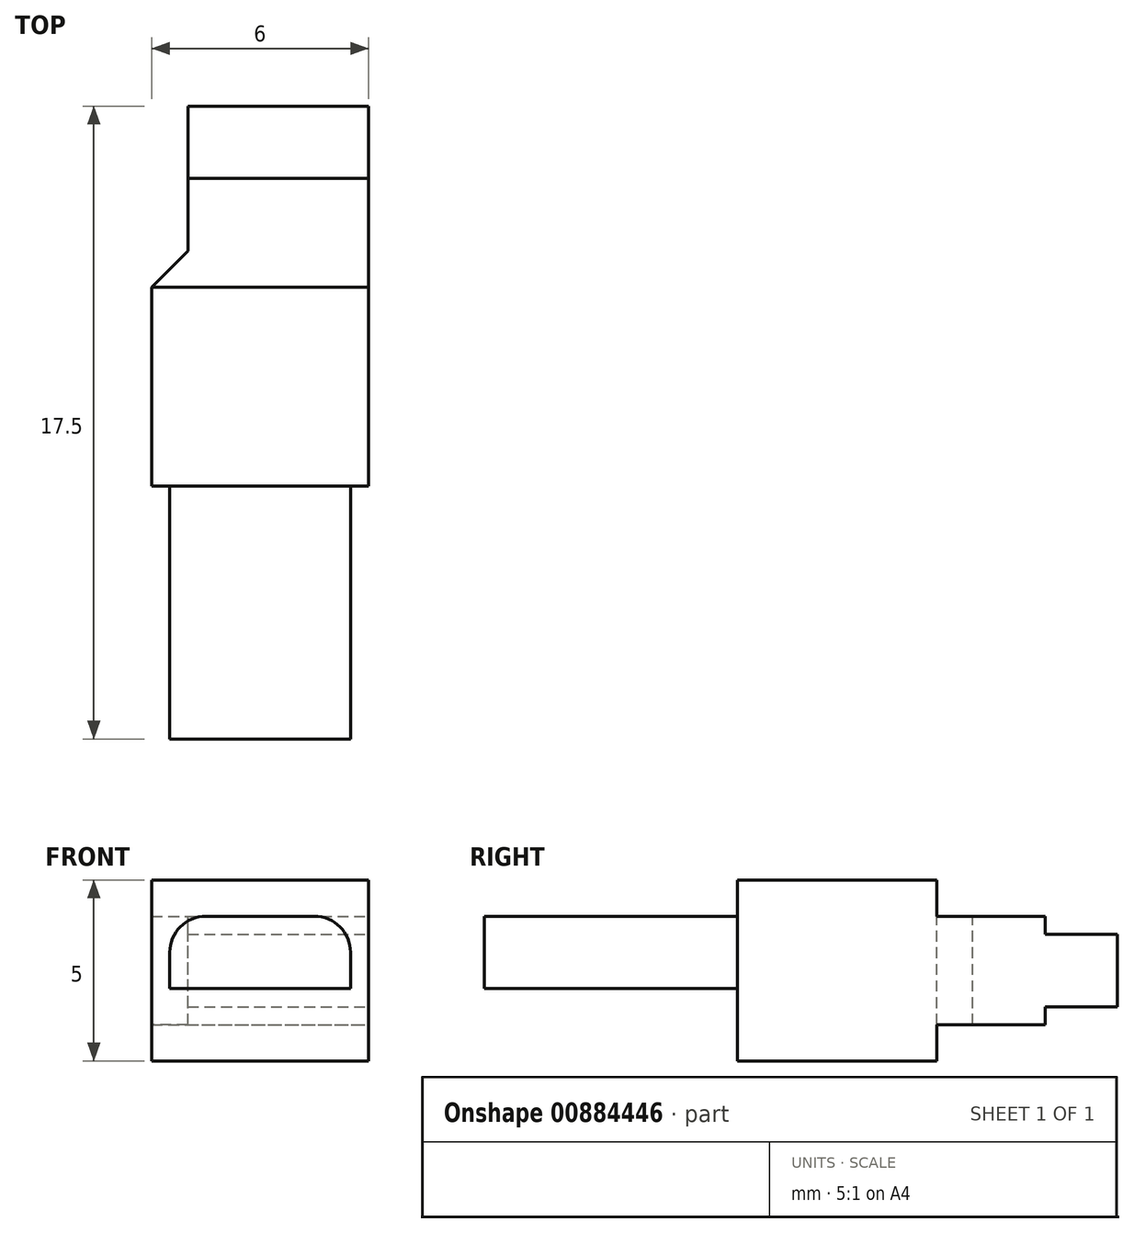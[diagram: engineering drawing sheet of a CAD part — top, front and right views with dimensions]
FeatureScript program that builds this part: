
annotation { "Feature Type Name" : "Feature", "Feature Type Description" : "" }
export const myFeature = defineFeature(function(context is Context, id is Id, definition is map)
    precondition{}
    {
        {
            var Q0;
            Q0=qCreatedBy(makeId("Front.planeOp"),FACE);
            var sketch = newSketch(context, id + "F0", { "sketchPlane" : qUnion([Q0])});
            skLineSegment(sketch, "E0.bottom", {"start": v(2.5, -1) * mm, "end": v(-2.5, -1) * mm});
            skLineSegment(sketch, "E0.top", {"start": v(1.5, 1) * mm, "end": v(-1.5, 1) * mm});
            skLineSegment(sketch, "E0.left", {"start": v(2.5, -1) * mm, "end": v(2.5, 0) * mm});
            skLineSegment(sketch, "E0.right", {"start": v(-2.5, -1) * mm, "end": v(-2.5, 0) * mm});
            skPoint(sketch, "E0.middle", {"position": v(0, 0) * mm});
            skPoint(sketch, "E1.visualSharp", {"position": v(-2.5, 1) * mm});
            skArc(sketch, "E1.filletArc", {"start": v(-1.5, 1) * mm, "mid": v(-2.2, 0.7) * mm, "end": v(-2.5, 0) * mm});
            skPoint(sketch, "E2.visualSharp", {"position": v(2.5, 1) * mm});
            skArc(sketch, "E2.filletArc", {"start": v(2.5, 0) * mm, "mid": v(2.2, 0.7) * mm, "end": v(1.5, 1) * mm});
            skSolve(sketch);
        }
        {
            var Q0;
            Q0=makeQuery(id+"F0.imprint","IMPRINT",FACE,{"disambiguationData":[TD([[makeQuery(id+"F0.imprint","IMPRINT",EDGE,{"derivedFrom":sQuery(id+"F0.wireOp",EDGE,"E0.bottom")}),-1.0]])]});
            extrude(context, id + "F1", {"entities" : qUnion([Q0]), "depth" : 7 * mm, "offsetDistance" : 25 * mm});
        }
        {
            var Q0;
            Q0=makeQuery(id+"F1.opExtrude","CAP_FACE",FACE,{"disambiguationData":[OSD([sQuery(id+"F0.wireOp",EDGE,"E0.bottom"),sQuery(id+"F0.wireOp",EDGE,"E0.top"),sQuery(id+"F0.wireOp",EDGE,"E0.left"),sQuery(id+"F0.wireOp",EDGE,"E0.right"),sQuery(id+"F0.wireOp",EDGE,"E1.filletArc"),sQuery(id+"F0.wireOp",EDGE,"E2.filletArc")])],"isStart":true});
            var sketch = newSketch(context, id + "F2", { "sketchPlane" : qUnion([Q0])});
            skLineSegment(sketch, "E3.bottom", {"start": v(3, -3) * mm, "end": v(-3, -3) * mm});
            skLineSegment(sketch, "E3.top", {"start": v(3, 2) * mm, "end": v(-3, 2) * mm});
            skLineSegment(sketch, "E3.left", {"start": v(3, -3) * mm, "end": v(3, 2) * mm});
            skLineSegment(sketch, "E3.right", {"start": v(-3, -3) * mm, "end": v(-3, 2) * mm});
            skPoint(sketch, "E3.middle", {"position": v(0, -0.5) * mm});
            skSolve(sketch);
        }
        {
            var Q0;
            Q0=makeQuery(id+"F2.imprint","IMPRINT",FACE,{"disambiguationData":[TD([[makeQuery(id+"F2.imprint","IMPRINT",EDGE,{"derivedFrom":sQuery(id+"F2.wireOp",EDGE,"E3.bottom")}),-1.0]])]});
            var Q1;
            Q1=makeQuery(id+"F2.imprint","IMPRINT",FACE,{"disambiguationData":[TD([[makeQuery(id+"F2.imprint","IMPRINT",EDGE,{"derivedFrom":makeQuery(id+"F1.opExtrude","CAP_EDGE",EDGE,{"disambiguationData":[OSD([sQuery(id+"F0.wireOp",EDGE,"E0.bottom")])],"isStart":true})}),1.0]])]});
            extrude(context, id + "F3", {"entities" : qUnion([Q0, Q1]), "operationType" : NewBodyOperationType.ADD, "depth" : 5.5 * mm, "offsetDistance" : 25 * mm});
        }
        {
            var Q0;
            Q0=makeQuery(id+"F3.opExtrude","CAP_FACE",FACE,{"disambiguationData":[OSD([sQuery(id+"F2.wireOp",EDGE,"E3.bottom"),sQuery(id+"F2.wireOp",EDGE,"E3.top"),sQuery(id+"F2.wireOp",EDGE,"E3.left"),sQuery(id+"F2.wireOp",EDGE,"E3.right")])],"isStart":false});
            var sketch = newSketch(context, id + "F4", { "sketchPlane" : qUnion([Q0])});
            skLineSegment(sketch, "E4", {"start": v(3, -0.5) * mm, "end": v(-3, -0.5) * mm, "construction": true});
            skLineSegment(sketch, "E5.bottom", {"start": v(3, 1) * mm, "end": v(-3, 1) * mm});
            skLineSegment(sketch, "E5.top", {"start": v(3, -2) * mm, "end": v(-3, -2) * mm});
            skLineSegment(sketch, "E5.left", {"start": v(3, 1) * mm, "end": v(3, -2) * mm});
            skLineSegment(sketch, "E5.right", {"start": v(-3, 1) * mm, "end": v(-3, -2) * mm});
            skPoint(sketch, "E5.middle", {"position": v(0, -0.5) * mm});
            skSolve(sketch);
        }
        {
            var Q0;
            Q0=makeQuery(id+"F4.imprint","IMPRINT",FACE,{"disambiguationData":[TD([[makeQuery(id+"F4.imprint","IMPRINT",EDGE,{"derivedFrom":sQuery(id+"F4.wireOp",EDGE,"E5.bottom")}),1.0]])]});
            extrude(context, id + "F5", {"entities" : qUnion([Q0]), "operationType" : NewBodyOperationType.ADD, "depth" : 3 * mm, "offsetDistance" : 25 * mm});
        }
        {
            var Q0;
            Q0=makeQuery(id+"F5.opExtrude","CAP_FACE",FACE,{"disambiguationData":[OSD([sQuery(id+"F4.wireOp",EDGE,"E5.bottom"),sQuery(id+"F4.wireOp",EDGE,"E5.top"),sQuery(id+"F4.wireOp",EDGE,"E5.left"),sQuery(id+"F4.wireOp",EDGE,"E5.right")])],"isStart":false});
            var sketch = newSketch(context, id + "F6", { "sketchPlane" : qUnion([Q0])});
            skLineSegment(sketch, "E6", {"start": v(-3, -0.5) * mm, "end": v(3, -0.5) * mm, "construction": true});
            skLineSegment(sketch, "E7.bottom", {"start": v(3, -1.5) * mm, "end": v(-3, -1.5) * mm});
            skLineSegment(sketch, "E7.top", {"start": v(3, 0.5) * mm, "end": v(-3, 0.5) * mm});
            skLineSegment(sketch, "E7.left", {"start": v(3, -1.5) * mm, "end": v(3, 0.5) * mm});
            skLineSegment(sketch, "E7.right", {"start": v(-3, -1.5) * mm, "end": v(-3, 0.5) * mm});
            skPoint(sketch, "E7.middle", {"position": v(0, -0.5) * mm});
            skSolve(sketch);
        }
        {
            var Q0;
            Q0=makeQuery(id+"F6.imprint","IMPRINT",FACE,{"disambiguationData":[TD([[makeQuery(id+"F6.imprint","IMPRINT",EDGE,{"derivedFrom":sQuery(id+"F6.wireOp",EDGE,"E7.bottom")}),-1.0]])]});
            extrude(context, id + "F7", {"entities" : qUnion([Q0]), "operationType" : NewBodyOperationType.ADD, "depth" : 2 * mm, "offsetDistance" : 25 * mm});
        }
        {
            var Q0;
            Q0=makeQuery(id+"F7.boolean.opBoolean","MERGE",FACE,{"derivedFrom":[makeQuery(id+"F5.boolean.opBoolean","MERGE",FACE,{"derivedFrom":[makeQuery(id+"F3.opExtrude","SWEPT_FACE",FACE,{"disambiguationData":[OSD([sQuery(id+"F2.wireOp",EDGE,"E3.left")])]}),makeQuery(id+"F5.opExtrude","SWEPT_FACE",FACE,{"disambiguationData":[OSD([sQuery(id+"F4.wireOp",EDGE,"E5.left")])]})]}),makeQuery(id+"F7.opExtrude","SWEPT_FACE",FACE,{"disambiguationData":[OSD([sQuery(id+"F6.wireOp",EDGE,"E7.left")])]})]});
            var sketch = newSketch(context, id + "F8", { "sketchPlane" : qUnion([Q0])});
            skLineSegment(sketch, "E8.bottom", {"start": v(-5.5, 1) * mm, "end": v(-10.5, 1) * mm});
            skLineSegment(sketch, "E8.top", {"start": v(-5.5, -2) * mm, "end": v(-10.5, -2) * mm});
            skLineSegment(sketch, "E8.left", {"start": v(-5.5, 1) * mm, "end": v(-5.5, -2) * mm});
            skLineSegment(sketch, "E8.right", {"start": v(-10.5, 1) * mm, "end": v(-10.5, -2) * mm});
            skSolve(sketch);
        }
        {
            var Q0;
            {var subQ7=sQuery(id+"F8.wireOp",EDGE,"E8.left");Q0=makeQuery(id+"F8.imprint","IMPRINT",FACE,{"disambiguationData":[TD([[makeQuery(id+"F8.imprint","IMPRINT",EDGE,{"derivedFrom":subQ7}),-1.0]])]});}
            extrude(context, id + "F9", {"entities" : qUnion([Q0]), "operationType" : NewBodyOperationType.REMOVE, "oppositeDirection" : true, "depth" : 1 * mm, "offsetDistance" : 25 * mm});
        }
        {
            var Q0;
            Q0=makeQuery(id+"F9.boolean.opBoolean","COPY",EDGE,{"derivedFrom":makeQuery(id+"F9.opExtrude","CAP_EDGE",EDGE,{"disambiguationData":[OSD([sQuery(id+"F8.wireOp",EDGE,"E8.left")])],"isStart":false})});
            chamfer(context, id + "F10", {"entities" : qUnion([Q0]), "width" : 1 * mm, "tangentPropagation" : true});
        }
    });
